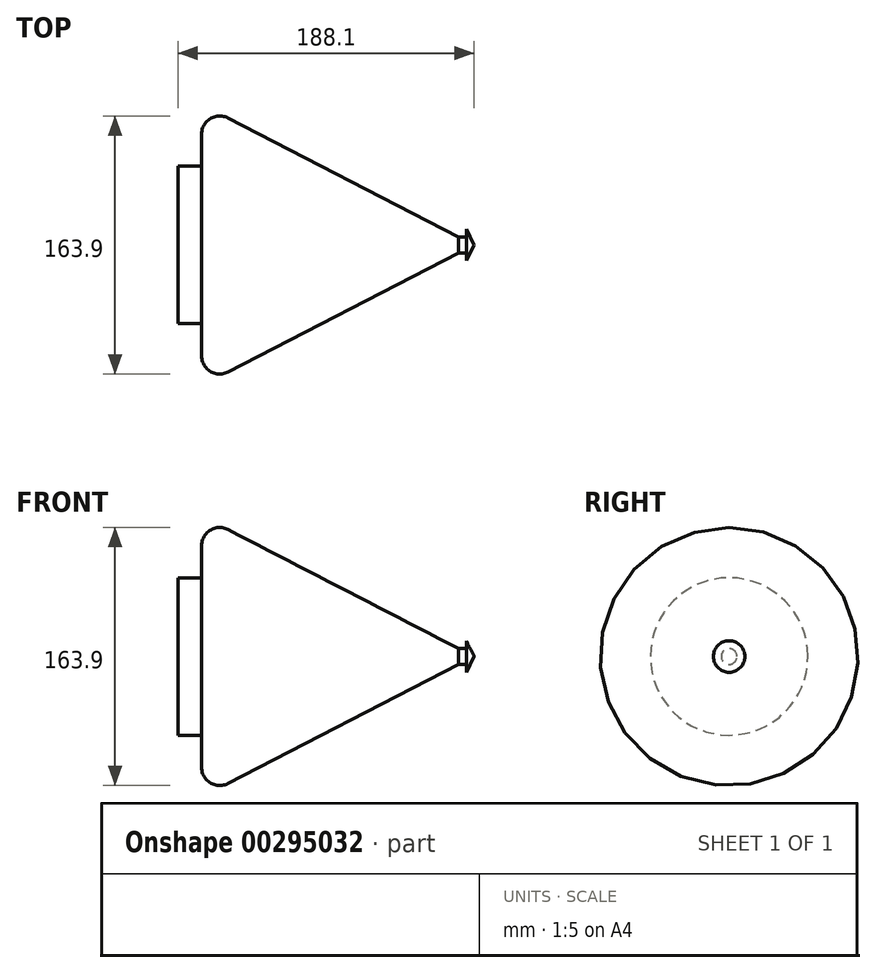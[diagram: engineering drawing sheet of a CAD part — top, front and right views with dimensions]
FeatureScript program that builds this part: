
annotation { "Feature Type Name" : "Feature", "Feature Type Description" : "" }
export const myFeature = defineFeature(function(context is Context, id is Id, definition is map)
    precondition{}
    {
        {
            var Q0;
            Q0=qCreatedBy(makeId("Front.planeOp"),FACE);
            var sketch = newSketch(context, id + "F0", { "sketchPlane" : qUnion([Q0])});
            skLineSegment(sketch, "E0.bottom", {"start": v(0, 0) * mm, "end": v(15, 0) * mm});
            skLineSegment(sketch, "E0.top", {"start": v(0, 50) * mm, "end": v(15, 50) * mm});
            skLineSegment(sketch, "E0.left", {"start": v(0, 0) * mm, "end": v(0, 50) * mm});
            skLineSegment(sketch, "E1.bottom", {"start": v(15, 0) * mm, "end": v(155, 0) * mm});
            skLineSegment(sketch, "E1.left", {"start": v(15, 50) * mm, "end": v(15, 70.44) * mm});
            skLineSegment(sketch, "E2.bottom", {"start": v(178.1, 5) * mm, "end": v(183.1, 5) * mm});
            skLineSegment(sketch, "E2.top", {"start": v(178.1, 0) * mm, "end": v(183.1, 0) * mm});
            skLineSegment(sketch, "E3", {"start": v(31.8, 80.66) * mm, "end": v(178.1, 5) * mm});
            skPoint(sketch, "E4.visualSharp", {"position": v(15, 89.34) * mm});
            skArc(sketch, "E4.filletArc", {"start": v(31.8, 80.66) * mm, "mid": v(20.52, 80.27) * mm, "end": v(15, 70.44) * mm});
            skLineSegment(sketch, "E5.bottom", {"start": v(183.1, 0) * mm, "end": v(188.1, 0) * mm});
            skLineSegment(sketch, "E5.left", {"start": v(183.1, 5) * mm, "end": v(183.1, 10) * mm});
            skLineSegment(sketch, "E6", {"start": v(183.1, 10) * mm, "end": v(188.1, 0) * mm});
            skLineSegment(sketch, "E7", {"start": v(155, 0) * mm, "end": v(178.1, 0) * mm});
            skSolve(sketch);
        }
        {
            var Q0;
            Q0=makeQuery(id+"F0.imprint","IMPRINT",FACE,{"disambiguationData":[TD([[makeQuery(id+"F0.imprint","IMPRINT",EDGE,{"derivedFrom":sQuery(id+"F0.wireOp",EDGE,"E0.bottom")}),1.0]])]});
            var Q1;
            Q1=sQuery(id+"F0.wireOp",EDGE,"E1.bottom");
            revolve(context, id + "F1", {"entities" : qUnion([Q0]), "axis" : qUnion([Q1]), "revolveType" : RevolveType.FULL});
        }
    });
